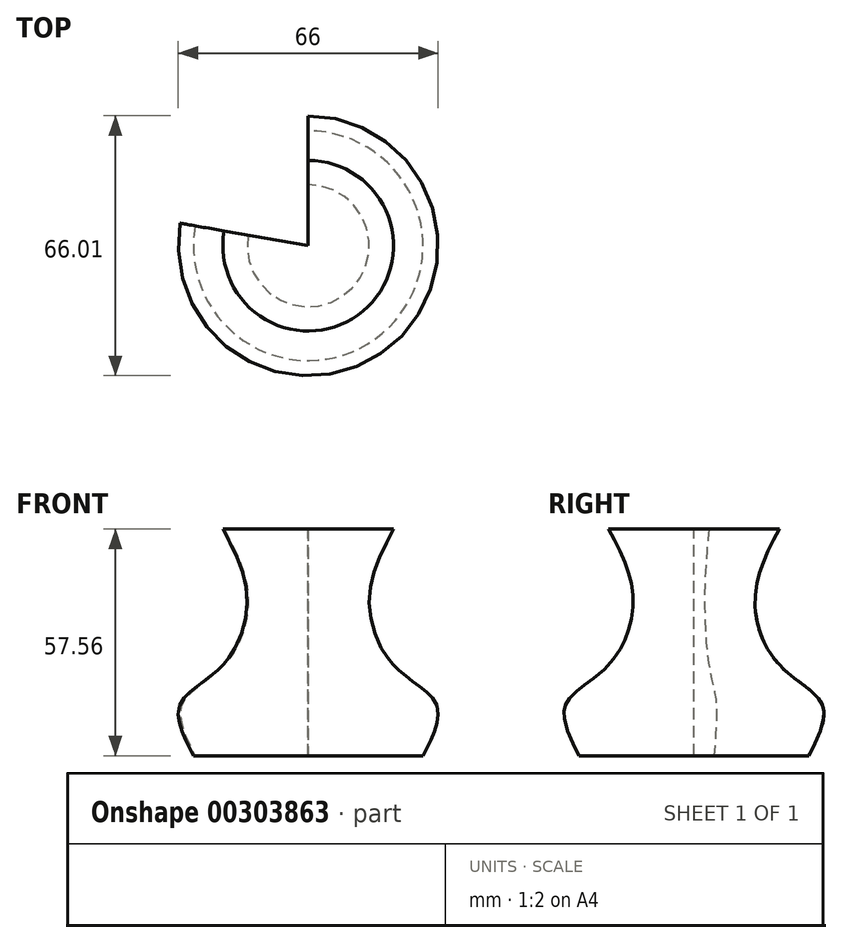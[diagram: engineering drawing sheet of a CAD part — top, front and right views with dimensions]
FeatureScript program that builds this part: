
annotation { "Feature Type Name" : "Feature", "Feature Type Description" : "" }
export const myFeature = defineFeature(function(context is Context, id is Id, definition is map)
    precondition{}
    {
        {
            var Q0;
            Q0=qCreatedBy(makeId("Right.planeOp"),FACE);
            var sketch = newSketch(context, id + "F0", { "sketchPlane" : qUnion([Q0])});
            skLineSegment(sketch, "E0", {"start": v(0, 0) * mm, "end": v(0, 57.56) * mm});
            skLineSegment(sketch, "E1", {"start": v(0, 57.56) * mm, "end": v(21.68, 57.56) * mm});
            skLineSegment(sketch, "E2", {"start": v(0, 0) * mm, "end": v(29.16, 0) * mm});
            skFitSpline(sketch, "E3", {"points": [v(21.68, 57.56) * mm, v(15.54, 40.68) * mm, v(21.68, 23.02) * mm, v(32.62, 12.86) * mm, v(29.16, 0) * mm], "startDerivative": vector(-32.7, -61.58) * mm, "endDerivative": vector(-31.7, -61.92) * mm});
            skSolve(sketch);
        }
        {
            var Q0;
            Q0=makeQuery(id+"F0.imprint","IMPRINT",FACE,{"disambiguationData":[TD([[makeQuery(id+"F0.imprint","IMPRINT",EDGE,{"derivedFrom":sQuery(id+"F0.wireOp",EDGE,"E0")}),-1.0]])]});
            var Q1;
            Q1=sQuery(id+"F0.wireOp",EDGE,"E0");
            revolve(context, id + "F1", {"entities" : qUnion([Q0]), "axis" : qUnion([Q1]), "revolveType" : RevolveType.ONE_DIRECTION, "oppositeDirection" : true, "angle" : 280 * degree});
        }
    });
